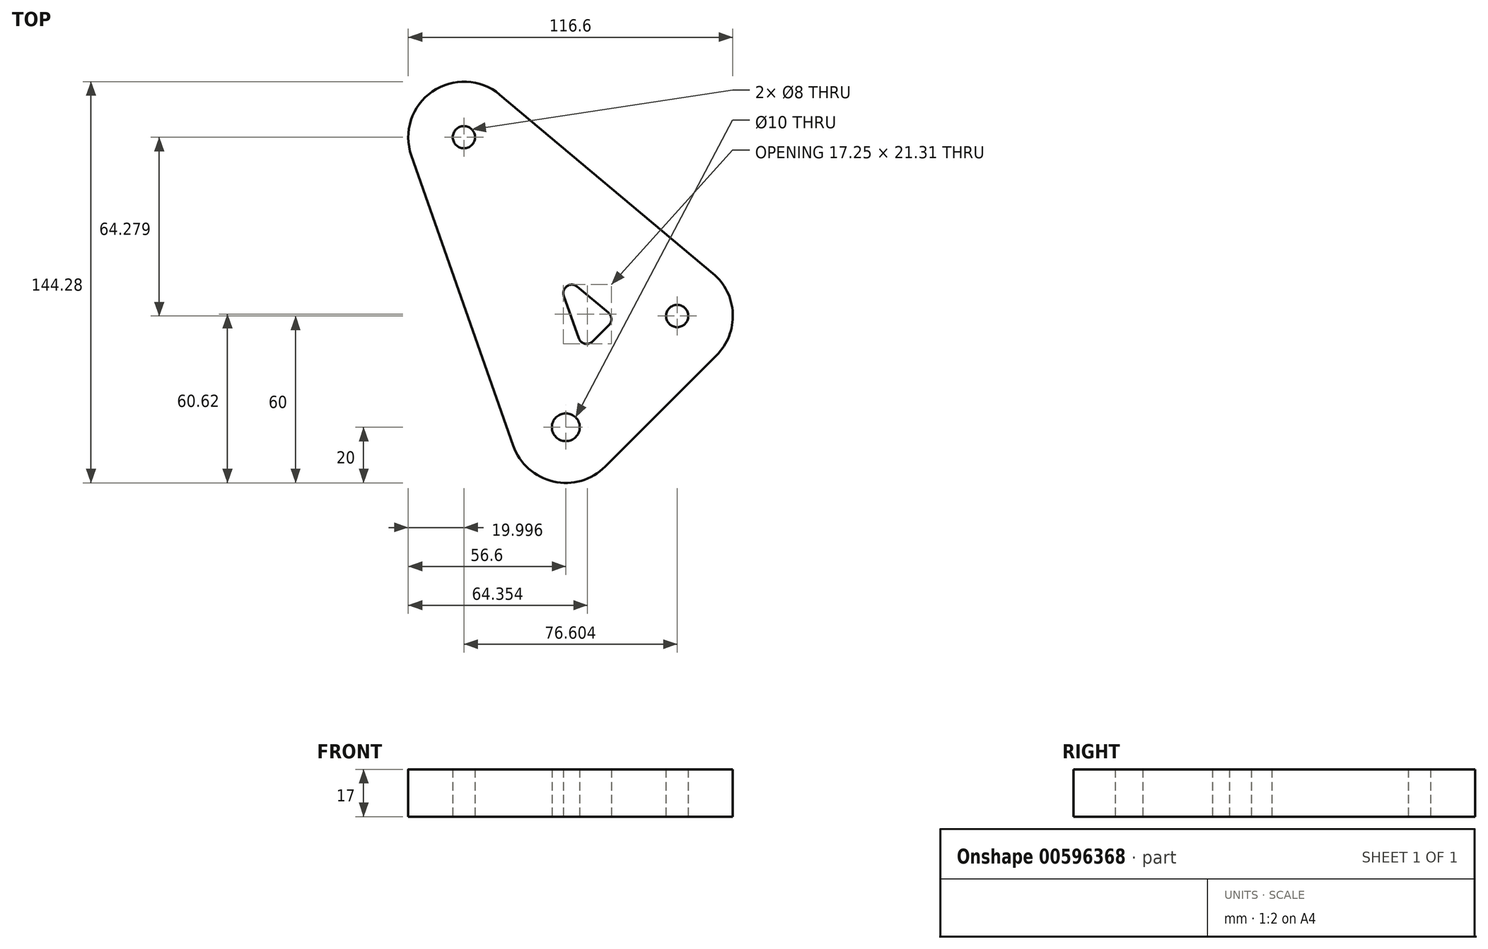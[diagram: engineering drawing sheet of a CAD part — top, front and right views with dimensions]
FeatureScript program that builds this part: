
annotation { "Feature Type Name" : "Feature", "Feature Type Description" : "" }
export const myFeature = defineFeature(function(context is Context, id is Id, definition is map)
    precondition{}
    {
        {
            var Q0;
            Q0=qCreatedBy(makeId("Top.planeOp"),FACE);
            var sketch = newSketch(context, id + "F0", { "sketchPlane" : qUnion([Q0])});
            skCircle(sketch, "E0", {"center": v(40, 0) * mm, "radius": 4 * mm});
            skCircle(sketch, "E1", {"center": v(0, -40) * mm, "radius": 5 * mm});
            skCircle(sketch, "E2", {"center": v(-36.6, 64.28) * mm, "radius": 4 * mm});
            skLineSegment(sketch, "E3", {"start": v(40, 0) * mm, "end": v(-36.6, 64.28) * mm, "construction": true});
            skLineSegment(sketch, "E4", {"start": v(40, 0) * mm, "end": v(0, -40) * mm, "construction": true});
            skLineSegment(sketch, "E5", {"start": v(-36.6, 64.28) * mm, "end": v(0, -40) * mm, "construction": true});
            skLineSegment(sketch, "E6.0", {"start": v(-55.48, 57.65) * mm, "end": v(-18.87, -46.62) * mm});
            skLineSegment(sketch, "E6.1", {"start": v(52.86, 15.32) * mm, "end": v(-23.75, 79.6) * mm});
            skLineSegment(sketch, "E6.2", {"start": v(54.14, -14.14) * mm, "end": v(14.14, -54.14) * mm});
            skPoint(sketch, "E7.visualSharp", {"position": v(-79.64, 126.5) * mm});
            skArc(sketch, "E7.filletArc", {"start": v(-23.75, 79.6) * mm, "mid": v(-47.98, 80.73) * mm, "end": v(-55.48, 57.65) * mm});
            skPoint(sketch, "E8.visualSharp", {"position": v(-8.34, -76.62) * mm});
            skArc(sketch, "E8.filletArc", {"start": v(-18.87, -46.62) * mm, "mid": v(-4.44, -59.5) * mm, "end": v(14.14, -54.14) * mm});
            skPoint(sketch, "E9.visualSharp", {"position": v(69.58, 1.3) * mm});
            skArc(sketch, "E9.filletArc", {"start": v(54.14, -14.14) * mm, "mid": v(59.98, 0.87) * mm, "end": v(52.86, 15.32) * mm});
            skLineSegment(sketch, "E10.0", {"start": v(15.31, 1.14) * mm, "end": v(4.06, 10.58) * mm});
            skLineSegment(sketch, "E10.1", {"start": v(15.5, -3.28) * mm, "end": v(9.63, -9.16) * mm});
            skLineSegment(sketch, "E10.2", {"start": v(-0.7, 7.29) * mm, "end": v(4.68, -8.03) * mm});
            skPoint(sketch, "E11.visualSharp", {"position": v(-4.33, 17.61) * mm});
            skArc(sketch, "E11.filletArc", {"start": v(4.06, 10.58) * mm, "mid": v(0.42, 10.75) * mm, "end": v(-0.7, 7.29) * mm});
            skPoint(sketch, "E12.visualSharp", {"position": v(17.82, -0.97) * mm});
            skArc(sketch, "E12.filletArc", {"start": v(15.5, -3.28) * mm, "mid": v(16.38, -1.03) * mm, "end": v(15.31, 1.14) * mm});
            skPoint(sketch, "E13.visualSharp", {"position": v(6.26, -12.53) * mm});
            skArc(sketch, "E13.filletArc", {"start": v(4.68, -8.03) * mm, "mid": v(6.84, -9.96) * mm, "end": v(9.63, -9.16) * mm});
            skSolve(sketch);
        }
        {
            var Q0;
            Q0=makeQuery(id+"F0.imprint","IMPRINT",FACE,{"disambiguationData":[TD([[makeQuery(id+"F0.imprint","IMPRINT",EDGE,{"derivedFrom":sQuery(id+"F0.wireOp",EDGE,"E0")}),-1.0]])]});
            extrude(context, id + "F1", {"entities" : qUnion([Q0]), "endBound" : BoundingType.SYMMETRIC, "depth" : 17 * mm, "offsetDistance" : 25 * mm});
        }
    });
